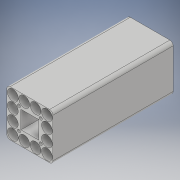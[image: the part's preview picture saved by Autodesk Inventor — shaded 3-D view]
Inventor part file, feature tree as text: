
AUTODESK INVENTOR PART (.ipt)
format: ipt  version: 2019.3 (Build 233278000, 278)  size: 197,120 bytes
history: native  units: mm
features: extrude x3, sketch x3, fillet x1
ambient origin geometry x8: Origin, YZ Plane, XZ Plane, XY Plane, X Axis, Y Axis, Z Axis, Center Point
bodies: Solid1 (feature_tree)
feature tree (7):
  extrude  "Extrusion1"  Depth=2.0mm TaperAngle=0.0deg
  extrude  "Extrusion2"  Depth=16.075mm
  extrude  "Extrusion3"  Depth=5.0mm
  fillet  "Fillet1"  Radius=9.0mm
  sketch  "Sketch1"  dims[d0=26.67mm d2=2.0mm d3=0.0mm]
  sketch  "Sketch2"  dims[d4=16.075mm d5=16.075mm]
  sketch  "Sketch3"  dims[d6=16.075mm d7=16.075mm d8=9.0mm d9=9.0mm d10=9.0mm d11=9.0mm d12=9.0mm d13=17.0mm d14=17.0mm d15=17.0mm d16=69.0mm d17=16.075mm d18=16.075mm d19=16.075mm d20=16.075mm d21=16.075mm d22=16.075mm d23=16.075mm d24=16.075mm d25=17.0mm d26=17.0mm d27=17.0mm d28=17.0mm d29=17.0mm d30=17.0mm d31=17.0mm d32=17.0mm d33=17.0mm d34=9.0mm d35=9.0mm d36=9.0mm d37=9.0mm d38=9.0mm d39=9.0mm d40=9.0mm d41=177.8mm d42=0.0mm d43=4.5mm d44=3.0mm d45=3.0mm d46=3.0mm d47=3.0mm d48=3.0mm d49=3.0mm d50=3.0mm d51=3.0mm d52=15.0mm d53=0.0mm d54=5.0mm]
